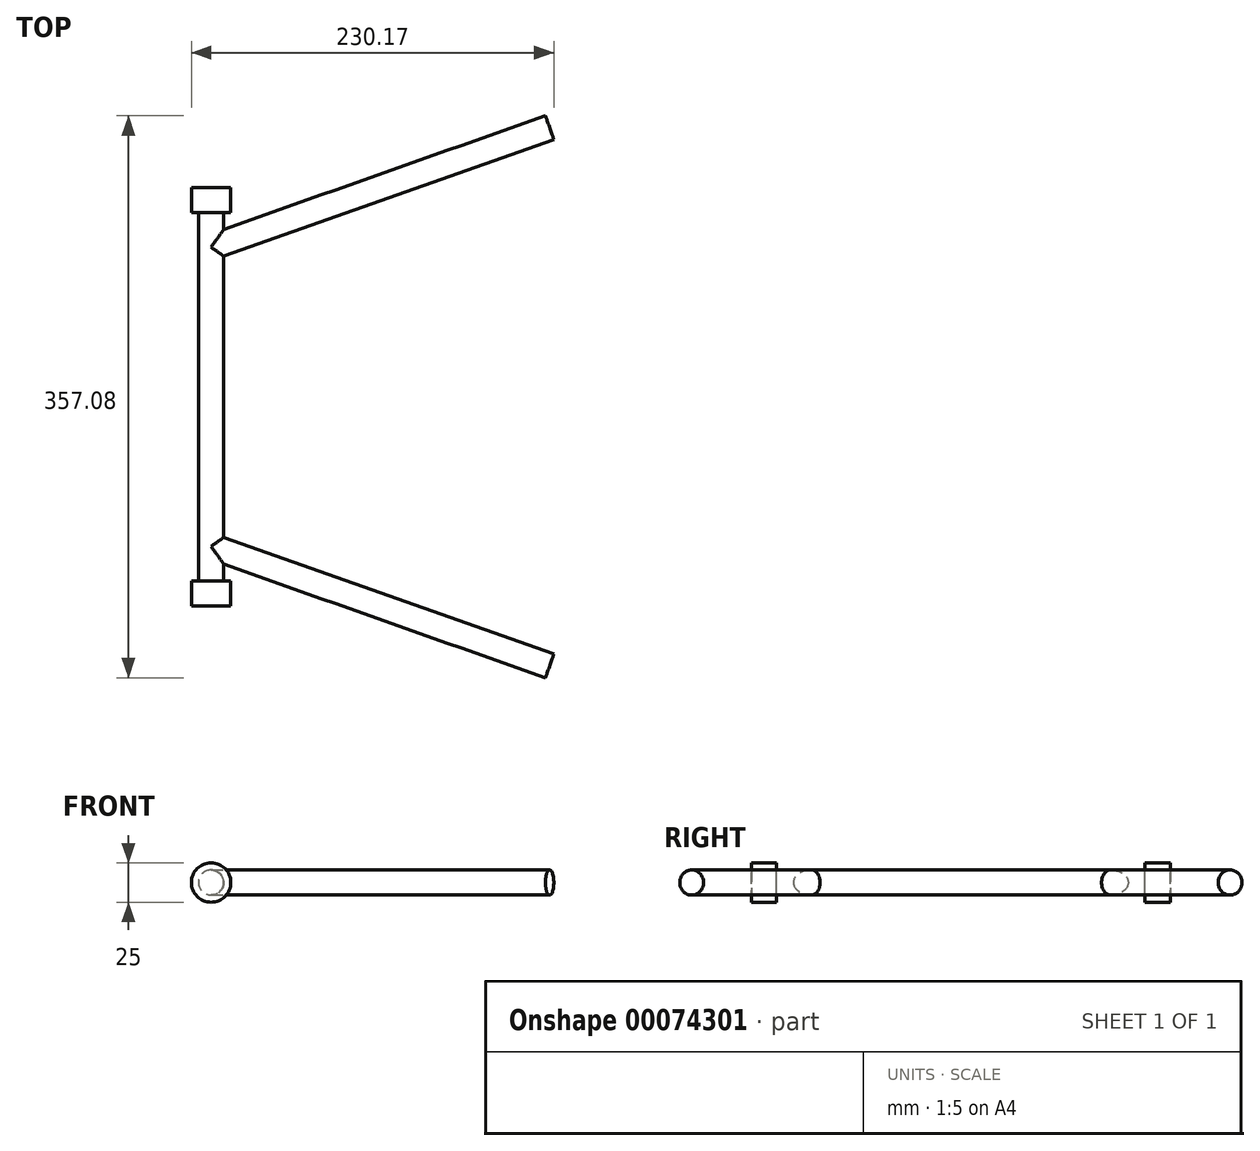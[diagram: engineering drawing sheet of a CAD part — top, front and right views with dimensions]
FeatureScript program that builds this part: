
annotation { "Feature Type Name" : "Feature", "Feature Type Description" : "" }
export const myFeature = defineFeature(function(context is Context, id is Id, definition is map)
    precondition{}
    {
        {
            var Q0;
            Q0=qCreatedBy(makeId("Front.planeOp"),FACE);
            var sketch = newSketch(context, id + "F0", { "sketchPlane" : qUnion([Q0])});
            skCircle(sketch, "E0", {"center": v(0, 0) * mm, "radius": 8 * mm});
            skSolve(sketch);
        }
        {
            var Q0;
            Q0 = qSketchRegion(id + "F0", true);
            extrude(context, id + "F1", {"entities" : qUnion([Q0]), "depth" : 234 * mm});
        }
        {
            var Q0;
            Q0=makeQuery(id+"F1.opExtrude","CAP_FACE",FACE,{"disambiguationData":[OSD([sQuery(id+"F0.wireOp",EDGE,"E0")])],"isStart":false});
            var sketch = newSketch(context, id + "F2", { "sketchPlane" : qUnion([Q0])});
            skCircle(sketch, "E1", {"center": v(0, 0) * mm, "radius": 12.5 * mm});
            skSolve(sketch);
        }
        {
            var Q0;
            Q0=makeQuery(id+"F2.imprint","IMPRINT",FACE,{"disambiguationData":[TD([[makeQuery(id+"F2.imprint","IMPRINT",EDGE,{"derivedFrom":makeQuery(id+"F1.opExtrude","CAP_EDGE",EDGE,{"disambiguationData":[OSD([sQuery(id+"F0.wireOp",EDGE,"E0")])],"isStart":false})}),1.0]])]});
            var Q1;
            Q1=makeQuery(id+"F2.imprint","IMPRINT",FACE,{"disambiguationData":[TD([[makeQuery(id+"F2.imprint","IMPRINT",EDGE,{"derivedFrom":sQuery(id+"F2.wireOp",EDGE,"E1")}),1.0]])]});
            extrude(context, id + "F3", {"entities" : qUnion([Q0, Q1]), "operationType" : NewBodyOperationType.ADD, "depth" : 16 * mm});
        }
        {
            var Q0;
            Q0=makeQuery(id+"F1.opExtrude","CAP_FACE",FACE,{"disambiguationData":[OSD([sQuery(id+"F0.wireOp",EDGE,"E0")])],"isStart":true});
            var sketch = newSketch(context, id + "F4", { "sketchPlane" : qUnion([Q0])});
            skCircle(sketch, "E2.0", {"center": v(0, 0) * mm, "radius": 12.5 * mm});
            skSolve(sketch);
        }
        {
            var Q0;
            Q0 = qSketchRegion(id + "F4", true);
            extrude(context, id + "F5", {"entities" : qUnion([Q0]), "operationType" : NewBodyOperationType.ADD, "depth" : 16 * mm});
        }
        {
            var Q0;
            Q0=qCreatedBy(makeId("Top.planeOp"),FACE);
            var sketch = newSketch(context, id + "F6", { "sketchPlane" : qUnion([Q0])});
            skLineSegment(sketch, "E3.0", {"start": v(-12.5, 0) * mm, "end": v(12.5, 0) * mm, "construction": true});
            skLineSegment(sketch, "E4", {"start": v(0, 0) * mm, "end": v(0, -44) * mm, "construction": true});
            skLineSegment(sketch, "E5", {"start": v(0, -22) * mm, "end": v(-13.95, -22) * mm, "construction": true});
            skLineSegment(sketch, "E6", {"start": v(215, -216.58) * mm, "end": v(215, 12.25) * mm, "construction": true});
            skLineSegment(sketch, "E7", {"start": v(0, -22) * mm, "end": v(215, 54) * mm});
            skSolve(sketch);
        }
        {
            var Q0;
            Q0=qCreatedBy(makeId("Top.planeOp"),FACE);
            var sketch = newSketch(context, id + "F7", { "sketchPlane" : qUnion([Q0])});
            skLineSegment(sketch, "E8.0", {"start": v(12.5, -234) * mm, "end": v(-12.5, -234) * mm, "construction": true});
            skLineSegment(sketch, "E9.bottom", {"start": v(-40.32, -117) * mm, "end": v(55, -117) * mm});
            skLineSegment(sketch, "E9.top", {"start": v(-40.32, -269.7) * mm, "end": v(55, -269.7) * mm});
            skLineSegment(sketch, "E9.left", {"start": v(-40.32, -117) * mm, "end": v(-40.32, -269.7) * mm});
            skLineSegment(sketch, "E9.right", {"start": v(55, -117) * mm, "end": v(55, -269.7) * mm});
            skSolve(sketch);
        }
        {
            var Q0;
            Q0 = qSketchRegion(id + "F7", true);
            extrude(context, id + "F8", {"entities" : qUnion([Q0]), "operationType" : NewBodyOperationType.REMOVE, "oppositeDirection" : true, "depth" : 100 * mm, "symmetric" : true});
        }
        {
            var Q0;
            Q0=sQuery(id+"F6.wireOp",VERTEX,"E5.start");
            var Q1;
            Q1=sQuery(id+"F6.wireOp",EDGE,"E7");
            cPlane(context, id + "F9", {"entities" : qUnion([Q0, Q1]), "cplaneType" : CPlaneType.LINE_POINT, "offset" : 25 * mm, "width" : 150 * mm, "height" : 150 * mm});
        }
        {
            var Q0;
            Q0=qCreatedBy(id+"F9.planeOp",FACE);
            var sketch = newSketch(context, id + "F10", { "sketchPlane" : qUnion([Q0])});
            skCircle(sketch, "E10", {"center": v(-20.74, 0) * mm, "radius": 8 * mm});
            skLineSegment(sketch, "E11.0", {"start": v(-20.74, 0) * mm, "end": v(-16.1, 0) * mm, "construction": true});
            skSolve(sketch);
        }
        {
            var Q0;
            Q0 = qSketchRegion(id + "F10", true);
            var Q1;
            Q1=sQuery(id+"F6.wireOp",EDGE,"E7");
            sweep(context, id + "F11", {"operationType" : NewBodyOperationType.ADD, "profiles" : qUnion([Q0]), "path" : qUnion([Q1])});
        }
        {
            var Q0;
            Q0=makeQuery(id+"F1.opExtrude","SWEPT_BODY",BODY,{"disambiguationData":[OSD([sQuery(id+"F0.wireOp",EDGE,"E0")])]});
            var Q1;
            Q1=makeQuery(id+"F8.boolean.opBoolean","COPY",FACE,{"derivedFrom":makeQuery(id+"F8.opExtrude","SWEPT_FACE",FACE,{"disambiguationData":[OSD([sQuery(id+"F7.wireOp",EDGE,"E9.bottom")])]})});
            mirror(context, id + "F12", {"operationType" : NewBodyOperationType.ADD, "entities" : qUnion([Q0]), "mirrorPlane" : qUnion([Q1])});
        }
    });
